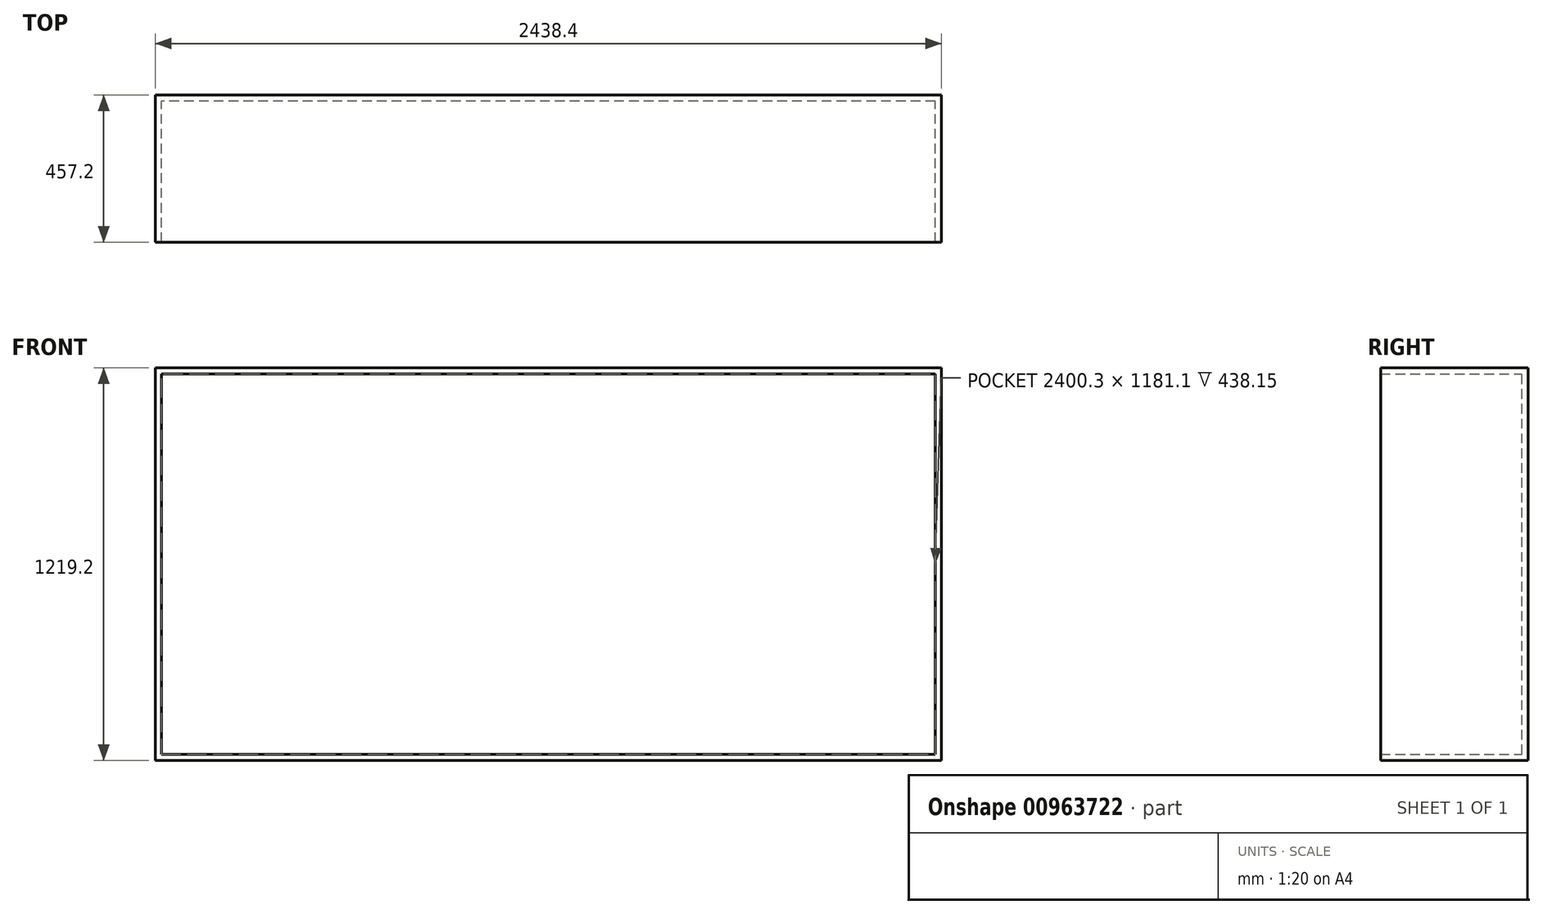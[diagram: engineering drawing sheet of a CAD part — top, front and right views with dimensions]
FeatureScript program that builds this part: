
annotation { "Feature Type Name" : "Feature", "Feature Type Description" : "" }
export const myFeature = defineFeature(function(context is Context, id is Id, definition is map)
    precondition{}
    {
        {
            var Q0;
            Q0=qCreatedBy(makeId("Front.planeOp"),FACE);
            var sketch = newSketch(context, id + "F0", { "sketchPlane" : qUnion([Q0])});
            skLineSegment(sketch, "E0.bottom", {"start": v(-906.83, 602.11) * mm, "end": v(1531.57, 602.11) * mm});
            skLineSegment(sketch, "E0.top", {"start": v(-906.83, -617.09) * mm, "end": v(1531.57, -617.09) * mm});
            skLineSegment(sketch, "E0.left", {"start": v(-906.83, 602.11) * mm, "end": v(-906.83, -617.09) * mm});
            skLineSegment(sketch, "E0.right", {"start": v(1531.57, 602.11) * mm, "end": v(1531.57, -617.09) * mm});
            skLineSegment(sketch, "E1.bottom", {"start": v(1512.52, -598.04) * mm, "end": v(-887.78, -598.04) * mm});
            skLineSegment(sketch, "E1.top", {"start": v(1512.52, 583.06) * mm, "end": v(-887.78, 583.06) * mm});
            skLineSegment(sketch, "E1.left", {"start": v(1512.52, -598.04) * mm, "end": v(1512.52, 583.06) * mm});
            skLineSegment(sketch, "E1.right", {"start": v(-887.78, -598.04) * mm, "end": v(-887.78, 583.06) * mm});
            skSolve(sketch);
        }
        {
            var Q0;
            Q0=makeQuery(id+"F0.imprint","IMPRINT",FACE,{"disambiguationData":[TD([[makeQuery(id+"F0.imprint","IMPRINT",EDGE,{"derivedFrom":sQuery(id+"F0.wireOp",EDGE,"E0.bottom")}),-1.0]])]});
            extrude(context, id + "F1", {"entities" : qUnion([Q0]), "depth" : 457.2 * mm, "offsetDistance" : 25.4 * mm});
        }
        {
            var Q0;
            Q0=makeQuery(id+"F1.opExtrude","CAP_FACE",FACE,{"disambiguationData":[OSD([sQuery(id+"F0.wireOp",EDGE,"E0.bottom"),sQuery(id+"F0.wireOp",EDGE,"E0.top"),sQuery(id+"F0.wireOp",EDGE,"E0.left"),sQuery(id+"F0.wireOp",EDGE,"E0.right"),sQuery(id+"F0.wireOp",EDGE,"E1.bottom"),sQuery(id+"F0.wireOp",EDGE,"E1.top"),sQuery(id+"F0.wireOp",EDGE,"E1.left"),sQuery(id+"F0.wireOp",EDGE,"E1.right")])],"isStart":true});
            var sketch = newSketch(context, id + "F2", { "sketchPlane" : qUnion([Q0])});
            skLineSegment(sketch, "E2.bottom", {"start": v(-1531.57, 602.11) * mm, "end": v(906.83, 602.11) * mm});
            skLineSegment(sketch, "E2.top", {"start": v(-1531.57, -617.09) * mm, "end": v(906.83, -617.09) * mm});
            skLineSegment(sketch, "E2.left", {"start": v(-1531.57, 602.11) * mm, "end": v(-1531.57, -617.09) * mm});
            skLineSegment(sketch, "E2.right", {"start": v(906.83, 602.11) * mm, "end": v(906.83, -617.09) * mm});
            skSolve(sketch);
        }
        {
            var Q0;
            Q0=makeQuery(id+"F2.imprint","IMPRINT",FACE,{"disambiguationData":[TD([[makeQuery(id+"F2.imprint","IMPRINT",EDGE,{"derivedFrom":makeQuery(id+"F1.opExtrude","CAP_EDGE",EDGE,{"disambiguationData":[OSD([sQuery(id+"F0.wireOp",EDGE,"E1.bottom")])],"isStart":true})}),1.0]])]});
            extrude(context, id + "F3", {"entities" : qUnion([Q0]), "operationType" : NewBodyOperationType.ADD, "oppositeDirection" : true, "depth" : 19.05 * mm, "offsetDistance" : 25.4 * mm});
        }
    });
